# Revit family: Sanitary_Showers_hansgrohe_Rainfinity-Hand-shower-130-3jet-26864000_NEW
name_source: partatom
category: Plumbing Fixtures
revit_build: Autodesk Revit 2015 (Build: 20140903_1530(x64)
units: mm (PartAtom-declared; Revit-internal decimal feet)

## types (2) — shared parameters
Always visible = Yes
BIMobject category = Showers
BIMobject category code = sanitary-showers
BIMobject main category = Sanitary
BIMobject main category code = sanitary
Brand url = http://www.hansgrohe-int.com
Date of publishing = 3/20/2019
Design country = Germany
Edition number = 1
GTIN code = https://4059625189696
IFC Classification = Sanitary Terminal
Installation instructions = https://www.hansgrohe.com
Manufacturer country = Germany
Manufacturer name = hansgrohe
Masterformat 2014 Code = 22 41 23
Masterformat 2014 Description = Residential Showers
Material 1 = Hansgrohe - Rainfinity - Graphite
Material main = Chrome
Material secondary = Chrome
NBS Reference Code = 35-06-81
NBS Reference Description = Shower Heads
OmniClass Code = 23-31 17 00
OmniClass Description = Showers
Product Guid = 6af33b3d-b01e-4842-b652-ca3a383ca3cb
Product SKU = 26864000
Product data url = https://bimobject.com
Product family = Rainfinity
Product group = Hand showers
Product name = Rainfinity Hand shower 130 3jet 26864000
Product url = https://www.hansgrohe.com
QR code = http://bimobject.com
Technical description = https://www.hansgrohe.com
UNSPSC Code = 30181503
Uniclass 1.4 Code = L7214
Uniclass 1.4 Description = Showers
Uniclass 2.0 Code = PR-35-06-81
Uniclass 2.0 Description = Shower Heads
Uniclass 2015 Code = Pr_40_20_87_76
Uniclass 2015 Name = Shower heads
Uniformat II Code = D2010
Uniformat II Description = Plumbing Fixtures

## per-type parameters (varying)
| type | Material 2 |
| 700 Matt White | Hansgrohe - Rainfinity - 700 Matt White |
| 000 Chrome | Hansgrohe - Rainfinity - 000 Chrome |

## geometry (parser evidence)
native form markers: Sweep x4
no freeform markers — native parametric forms only
